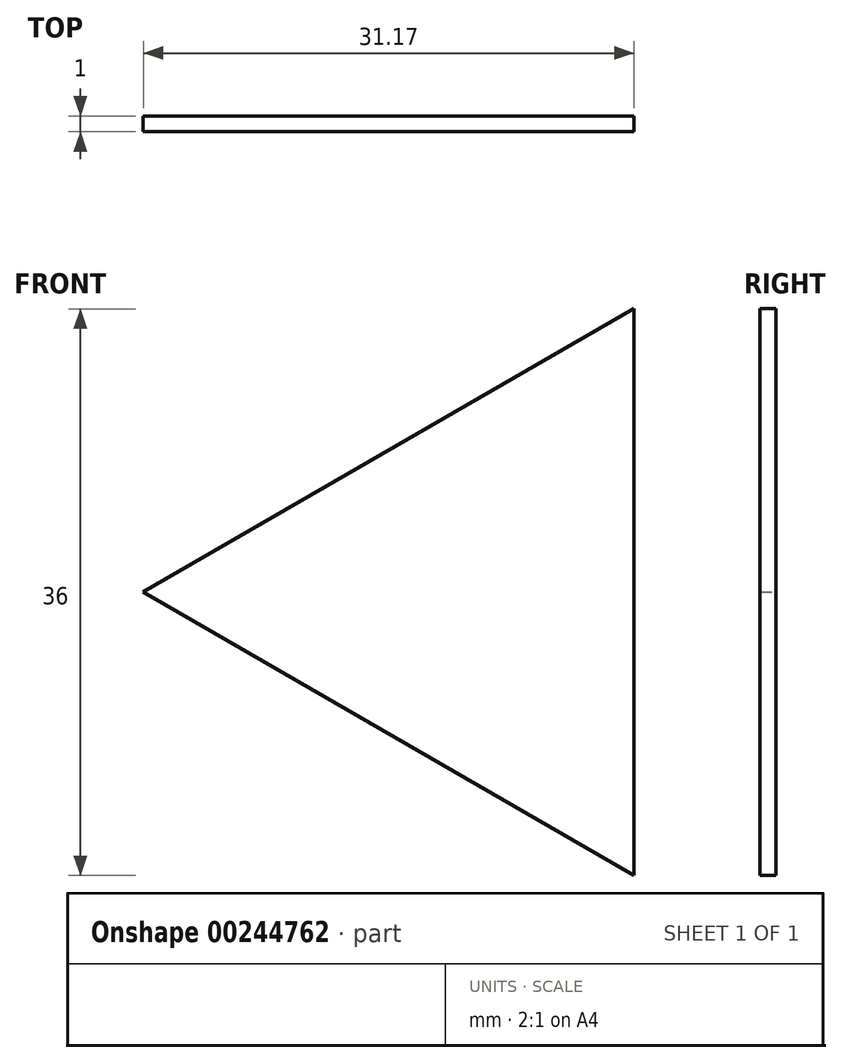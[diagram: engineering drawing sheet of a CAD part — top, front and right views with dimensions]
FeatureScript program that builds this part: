
annotation { "Feature Type Name" : "Feature", "Feature Type Description" : "" }
export const myFeature = defineFeature(function(context is Context, id is Id, definition is map)
    precondition{}
    {
        {
            var Q0;
            Q0=qCreatedBy(makeId("Front.planeOp"),FACE);
            var sketch = newSketch(context, id + "F0", { "sketchPlane" : qUnion([Q0])});
            skCircle(sketch, "E0.cCircle", {"center": v(-43.46, 14.58) * mm, "radius": 10.4 * mm, "construction": true});
            skLineSegment(sketch, "E0.0", {"start": v(-33.07, 32.58) * mm, "end": v(-33.07, -3.42) * mm});
            skLineSegment(sketch, "E0.1", {"start": v(-33.07, -3.42) * mm, "end": v(-64.24, 14.58) * mm});
            skLineSegment(sketch, "E0.2", {"start": v(-64.24, 14.58) * mm, "end": v(-33.07, 32.58) * mm});
            skPoint(sketch, "E0.0.midPoint", {"position": v(-33.07, 14.58) * mm});
            skSolve(sketch);
        }
        {
            var Q0;
            Q0=makeQuery(id+"F0.imprint","IMPRINT",FACE,{"disambiguationData":[TD([[makeQuery(id+"F0.imprint","IMPRINT",EDGE,{"derivedFrom":sQuery(id+"F0.wireOp",EDGE,"E0.0")}),-1.0]])]});
            extrude(context, id + "F1", {"entities" : qUnion([Q0]), "depth" : 1 * mm});
        }
    });
